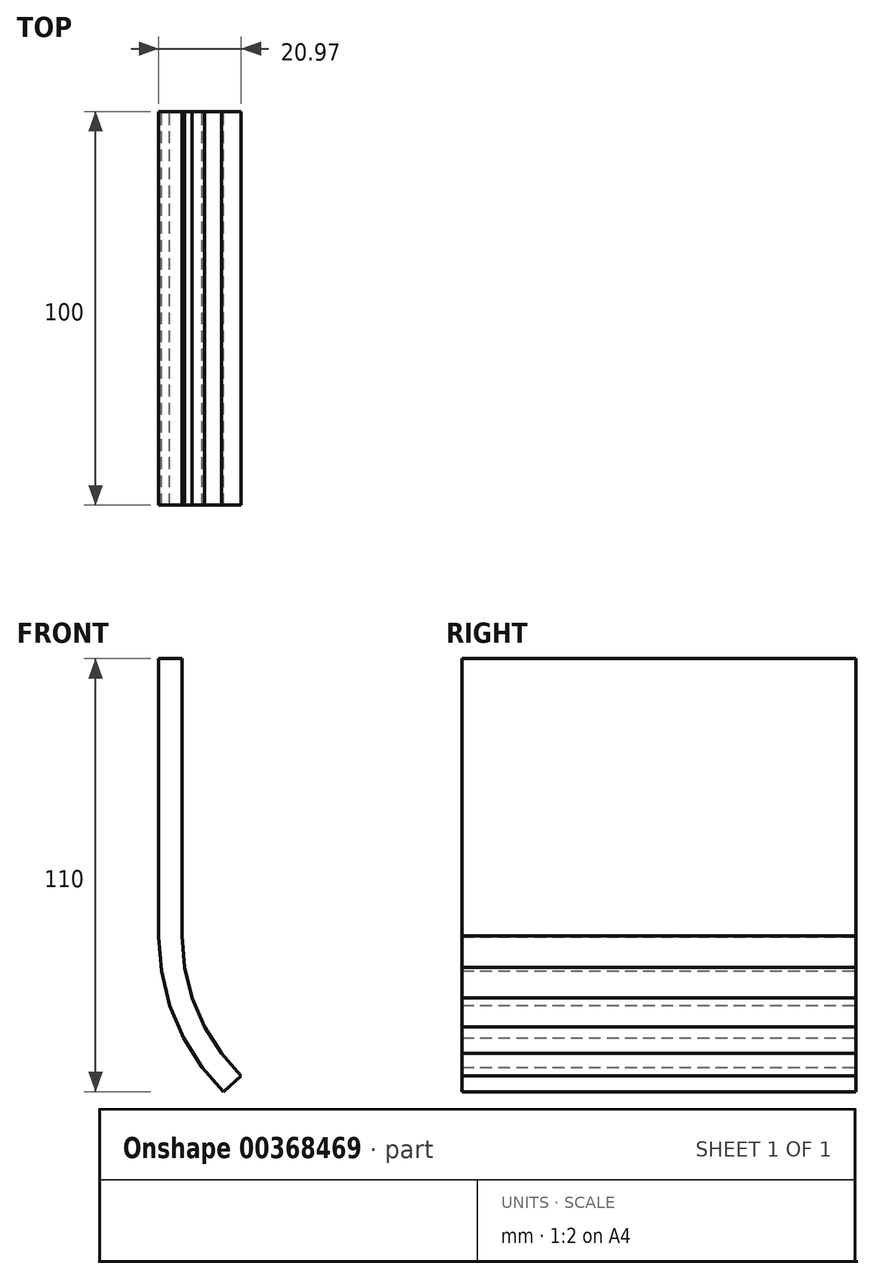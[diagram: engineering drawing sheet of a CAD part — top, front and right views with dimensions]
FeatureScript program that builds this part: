
annotation { "Feature Type Name" : "Feature", "Feature Type Description" : "" }
export const myFeature = defineFeature(function(context is Context, id is Id, definition is map)
    precondition{}
    {
        {
            var Q0;
            Q0=qCreatedBy(makeId("Front.planeOp"),FACE);
            var sketch = newSketch(context, id + "F0", { "sketchPlane" : qUnion([Q0])});
            skLineSegment(sketch, "E0", {"start": v(0, 0) * mm, "end": v(0, -70.4) * mm});
            skLineSegment(sketch, "E1", {"start": v(0, -70.4) * mm, "end": v(0, -110) * mm, "construction": true});
            skLineSegment(sketch, "E2", {"start": v(0, -110) * mm, "end": v(31.37, -110) * mm, "construction": true});
            skArc(sketch, "E3", {"start": v(0, -70.4) * mm, "mid": v(5.13, -92.46) * mm, "end": v(19.47, -110) * mm, "construction": true});
            skLineSegment(sketch, "E4", {"start": v(0, -70.4) * mm, "end": v(0.64, -78.37) * mm});
            skLineSegment(sketch, "E5", {"start": v(0.64, -78.37) * mm, "end": v(2.54, -86.14) * mm});
            skLineSegment(sketch, "E6", {"start": v(2.54, -86.14) * mm, "end": v(5.66, -93.51) * mm});
            skLineSegment(sketch, "E7", {"start": v(5.66, -93.51) * mm, "end": v(9.92, -100.29) * mm});
            skLineSegment(sketch, "E8", {"start": v(9.92, -100.29) * mm, "end": v(14.97, -106.04) * mm});
            skLineSegment(sketch, "E9.2", {"start": v(5.1, -103.89) * mm, "end": v(10.46, -110) * mm});
            skLineSegment(sketch, "E9.3", {"start": v(0.32, -96.3) * mm, "end": v(5.1, -103.89) * mm});
            skLineSegment(sketch, "E9.4", {"start": v(-6, 0) * mm, "end": v(-6, -70.64) * mm});
            skLineSegment(sketch, "E9.5", {"start": v(-6, -70.64) * mm, "end": v(-5.3, -79.33) * mm});
            skLineSegment(sketch, "E9.6", {"start": v(-5.3, -79.33) * mm, "end": v(-3.17, -88.04) * mm});
            skLineSegment(sketch, "E9.7", {"start": v(-3.17, -88.04) * mm, "end": v(0.32, -96.3) * mm});
            skLineSegment(sketch, "E10", {"start": v(0, 0) * mm, "end": v(-6, 0) * mm});
            skLineSegment(sketch, "E11", {"start": v(10.46, -110) * mm, "end": v(14.97, -106.04) * mm});
            skSolve(sketch);
        }
        {
            var Q0;
            Q0 = qSketchRegion(id + "F0", true);
            extrude(context, id + "F1", {"entities" : qUnion([Q0]), "depth" : 100 * mm});
        }
    });
